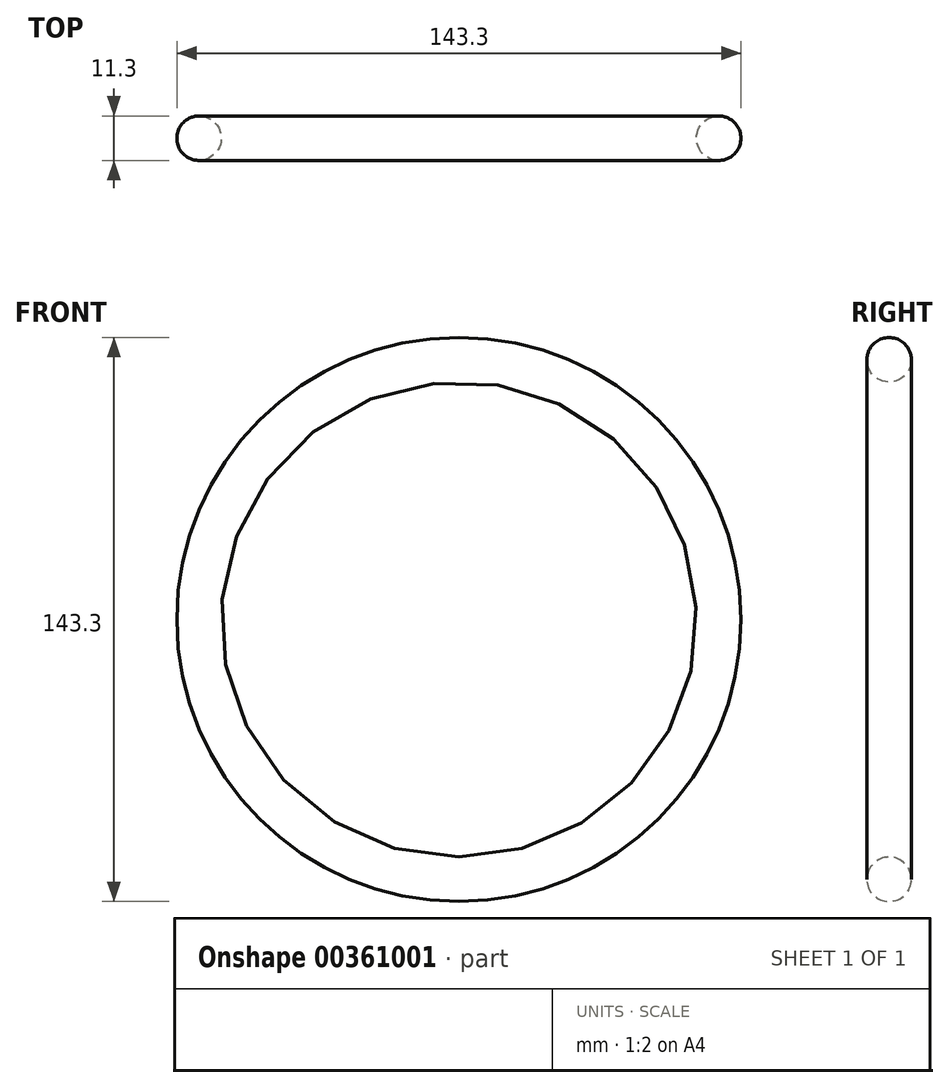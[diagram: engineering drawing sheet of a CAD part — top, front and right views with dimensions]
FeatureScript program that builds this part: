
annotation { "Feature Type Name" : "Feature", "Feature Type Description" : "" }
export const myFeature = defineFeature(function(context is Context, id is Id, definition is map)
    precondition{}
    {
        {
            var Q0;
            Q0=qCreatedBy(makeId("Front.planeOp"),FACE);
            var sketch = newSketch(context, id + "F0", { "sketchPlane" : qUnion([Q0])});
            skCircle(sketch, "E0", {"center": v(0, 0) * mm, "radius": 66 * mm});
            skPoint(sketch, "E1", {"position": v(0, -66) * mm});
            skSolve(sketch);
        }
        {
            var Q0;
            Q0=qCreatedBy(makeId("Right.planeOp"),FACE);
            var sketch = newSketch(context, id + "F1", { "sketchPlane" : qUnion([Q0])});
            skCircle(sketch, "E2", {"center": v(0, -66) * mm, "radius": 5.65 * mm});
            skSolve(sketch);
        }
        {
            var Q0;
            Q0=makeQuery(id+"F1.imprint","IMPRINT",FACE,{"disambiguationData":[TD([[makeQuery(id+"F1.imprint","IMPRINT",EDGE,{"derivedFrom":sQuery(id+"F1.wireOp",EDGE,"E2")}),1.0]])]});
            var Q1;
            Q1=sQuery(id+"F0.wireOp",EDGE,"E0");
            sweep(context, id + "F2", {"profiles" : qUnion([Q0]), "path" : qUnion([Q1])});
        }
    });
